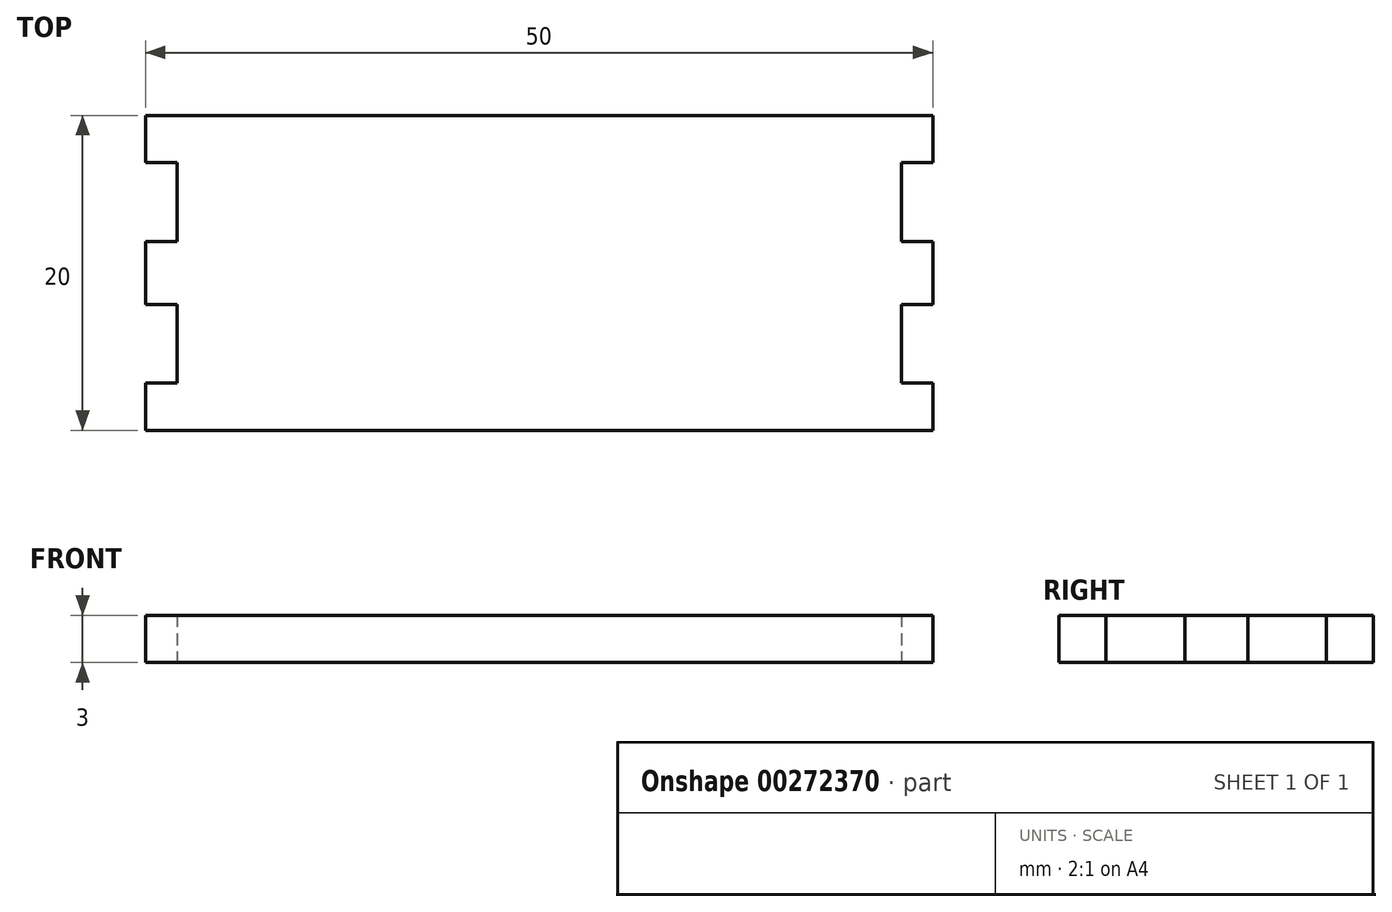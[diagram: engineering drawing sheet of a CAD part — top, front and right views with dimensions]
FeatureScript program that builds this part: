
annotation { "Feature Type Name" : "Feature", "Feature Type Description" : "" }
export const myFeature = defineFeature(function(context is Context, id is Id, definition is map)
    precondition{}
    {
        {
            var Q0;
            Q0=qCreatedBy(makeId("Top.planeOp"),FACE);
            var sketch = newSketch(context, id + "F0", { "sketchPlane" : qUnion([Q0])});
            skLineSegment(sketch, "E0.bottom", {"start": v(-25, 10) * mm, "end": v(25, 10) * mm});
            skLineSegment(sketch, "E0.top", {"start": v(-25, -10) * mm, "end": v(25, -10) * mm});
            skPoint(sketch, "E0.middle", {"position": v(0, 0) * mm});
            skLineSegment(sketch, "E1", {"start": v(0, 10) * mm, "end": v(0, -10) * mm, "construction": true});
            skLineSegment(sketch, "E2", {"start": v(-25, 0) * mm, "end": v(25, 0) * mm, "construction": true});
            skLineSegment(sketch, "E3", {"start": v(-25, 10) * mm, "end": v(-25, 7) * mm});
            skLineSegment(sketch, "E4", {"start": v(-25, 7) * mm, "end": v(-23, 7) * mm});
            skLineSegment(sketch, "E5", {"start": v(-23, 7) * mm, "end": v(-23, 2) * mm});
            skLineSegment(sketch, "E6", {"start": v(-23, 2) * mm, "end": v(-25, 2) * mm});
            skLineSegment(sketch, "E7", {"start": v(-25, 2) * mm, "end": v(-25, 0) * mm});
            skLineSegment(sketch, "E8.MirrorCS", {"start": v(-25, -2) * mm, "end": v(-25, 0) * mm});
            skLineSegment(sketch, "E9.MirrorCS", {"start": v(-23, -2) * mm, "end": v(-25, -2) * mm});
            skLineSegment(sketch, "E10.MirrorCS", {"start": v(-23, -7) * mm, "end": v(-23, -2) * mm});
            skLineSegment(sketch, "E11.MirrorCS", {"start": v(-25, -10) * mm, "end": v(-25, -7) * mm});
            skLineSegment(sketch, "E12.MirrorCS", {"start": v(-25, -7) * mm, "end": v(-23, -7) * mm});
            skLineSegment(sketch, "E13.MirrorCS", {"start": v(25, -10) * mm, "end": v(25, -7) * mm});
            skLineSegment(sketch, "E14.MirrorCS", {"start": v(25, -7) * mm, "end": v(23, -7) * mm});
            skLineSegment(sketch, "E15.MirrorCS", {"start": v(23, -7) * mm, "end": v(23, -2) * mm});
            skLineSegment(sketch, "E16.MirrorCS", {"start": v(23, -2) * mm, "end": v(25, -2) * mm});
            skLineSegment(sketch, "E17.MirrorCS", {"start": v(25, 2) * mm, "end": v(25, 0) * mm});
            skLineSegment(sketch, "E18.MirrorCS", {"start": v(25, -2) * mm, "end": v(25, 0) * mm});
            skLineSegment(sketch, "E19.MirrorCS", {"start": v(23, 2) * mm, "end": v(25, 2) * mm});
            skLineSegment(sketch, "E20.MirrorCS", {"start": v(23, 7) * mm, "end": v(23, 2) * mm});
            skLineSegment(sketch, "E21.MirrorCS", {"start": v(25, 10) * mm, "end": v(25, 7) * mm});
            skLineSegment(sketch, "E22.MirrorCS", {"start": v(25, 7) * mm, "end": v(23, 7) * mm});
            skSolve(sketch);
        }
        {
            var Q0;
            Q0=makeQuery(id+"F0.imprint","IMPRINT",FACE,{"disambiguationData":[TD([[makeQuery(id+"F0.imprint","IMPRINT",EDGE,{"derivedFrom":sQuery(id+"F0.wireOp",EDGE,"E0.bottom")}),-1.0]])]});
            extrude(context, id + "F1", {"entities" : qUnion([Q0]), "depth" : 3 * mm});
        }
    });
